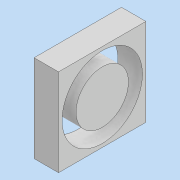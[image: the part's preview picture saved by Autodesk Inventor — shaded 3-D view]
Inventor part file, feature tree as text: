
AUTODESK INVENTOR PART (.ipt)
format: ipt  version: 2022 (Build 260153070, 153G)  size: 140,800 bytes
history: native  units: mm
features: other x2, extrude x2, plane x1, sketch x1
ambient origin geometry x8: Origin, YZ Plane, XZ Plane, XY Plane, X Axis, Y Axis, Z Axis, Center Point
bodies: Body1 (feature_tree)
feature tree (6):
  other  "P00173-09-002.ipt"
  plane  "Work Plane2"
  sketch  "Sketch3"  dims[d4=10.0mm d93=85.0mm d96=49.0mm d97=2.8mm d98=58.0mm d99=3.5mm d100=1.2mm d101=6.93mm d102=2.98mm d109=50.0mm d110=6.0mm d111=7.0mm d126=2.0mm d130=2.0mm d131=2.0mm d133=2.0mm d135=13.2mm d136=13.2mm d139=15.0mm d141=13.6mm d142=16.0mm d159=0.349066mm d160=3.5mm d161=1.5mm d162=3.5mm d163=16.580628mm d165=3.5mm d166=2.0mm d167=28.0mm d168=55.0mm d169=0.349066mm d170=0.349066mm d171=0.2mm d246=9.0mm d5=25.0mm d6=0.0mm d7=1.0mm d8=4.0mm d9=10.0mm d10=0.0mm]
  extrude  "Extrusion2"  Depth=25.0mm TaperAngle=0.0deg
  extrude  "Extrusion3"  Depth=10.0mm
  other  "Fan_Side"
